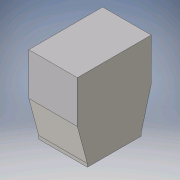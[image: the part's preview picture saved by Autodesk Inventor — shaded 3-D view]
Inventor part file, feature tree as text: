
AUTODESK INVENTOR PART (.ipt)
format: ipt  version: 2016 (Build 200138000, 138)  size: 131,584 bytes
history: native  units: in
note: dims shown in document units (in); Inventor stores cm internally (conversion verified against a paired STEP export)
features: sketch x4, extrude x3, hole x1, plane x1
ambient origin geometry x8: Origin, YZ Plane, XZ Plane, XY Plane, X Axis, Y Axis, Z Axis, Center Point
bodies: Solid1 (feature_tree)
feature tree (9):
  extrude  "Extrusion1"  Depth=2.0079in
  hole  "Hole1"  [1 undecoded]
  plane  "Work Plane1"
  extrude  "Extrusion3"  Depth=0.315in
  extrude  "Extrusion4"  Depth=1.6929in
  sketch  "Sketch1"  dims[d0=1.811in d1=2.0079in]
  sketch  "Sketch2"  dims[d2=0.1181in d3=0.0in d4=0.315in]
  sketch  "Sketch3"  dims[d5=0.315in d6=0.315in]
  sketch  "Sketch4"  dims[d7=0.315in d8=0.315in d9=0.315in d10=0.315in d11=0.315in d12=0.0787in d13=0.2362in d14=0.1575in d15=0.0787in d16=90.0deg d17=0.315in d18=0.8108in d19=7.874in d20=2.7559in d23=1.5748in d24=1.5748in d25=0.1181in d26=0.0in d27=0.1181in d28=0.1181in d29=0.1181in d30=0.1181in d31=0.1181in d32=1.6929in d33=0.0in]
note: 1 required parameter value undecoded (feature->parameter linkage not recoverable at this tier; creation-order binding heuristic only, values carry confidence <= 0.55)
